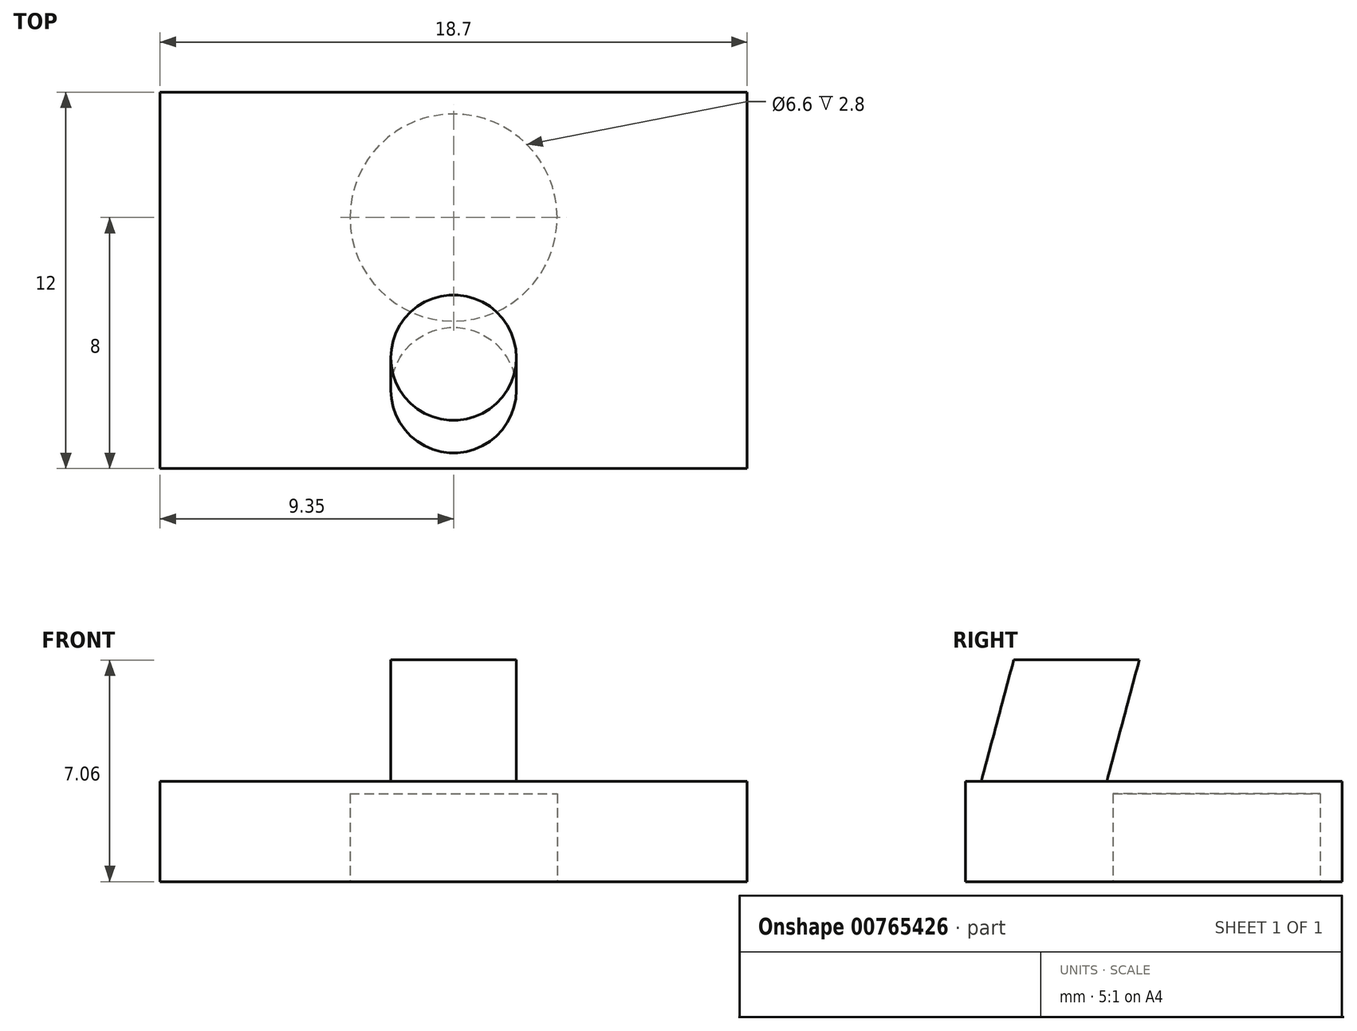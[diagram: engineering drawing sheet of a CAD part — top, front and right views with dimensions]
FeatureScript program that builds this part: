
annotation { "Feature Type Name" : "Feature", "Feature Type Description" : "" }
export const myFeature = defineFeature(function(context is Context, id is Id, definition is map)
    precondition{}
    {
        {
            var Q0;
            Q0=qCreatedBy(makeId("Top.planeOp"),FACE);
            var sketch = newSketch(context, id + "F0", { "sketchPlane" : qUnion([Q0])});
            skLineSegment(sketch, "E0.bottom", {"start": v(9.35, 6) * mm, "end": v(-9.35, 6) * mm});
            skLineSegment(sketch, "E0.top", {"start": v(9.35, -6) * mm, "end": v(-9.35, -6) * mm});
            skLineSegment(sketch, "E0.left", {"start": v(9.35, 6) * mm, "end": v(9.35, -6) * mm});
            skLineSegment(sketch, "E0.right", {"start": v(-9.35, 6) * mm, "end": v(-9.35, -6) * mm});
            skPoint(sketch, "E0.middle", {"position": v(0, 0) * mm});
            skSolve(sketch);
        }
        {
            var Q0;
            Q0 = qSketchRegion(id + "F0", true);
            extrude(context, id + "F1", {"entities" : qUnion([Q0]), "depth" : 3.2 * mm, "offsetDistance" : 25 * mm});
        }
        {
            var Q0;
            Q0=makeQuery(id+"F1.opExtrude","CAP_FACE",FACE,{"disambiguationData":[OSD([sQuery(id+"F0.wireOp",EDGE,"E0.bottom"),sQuery(id+"F0.wireOp",EDGE,"E0.top"),sQuery(id+"F0.wireOp",EDGE,"E0.left"),sQuery(id+"F0.wireOp",EDGE,"E0.right")])],"isStart":false});
            var sketch = newSketch(context, id + "F2", { "sketchPlane" : qUnion([Q0])});
            skCircle(sketch, "E1", {"center": v(0, -3.5) * mm, "radius": 2 * mm});
            skSolve(sketch);
        }
        {
            var Q0;
            Q0=makeQuery(id+"F1.opExtrude","CAP_FACE",FACE,{"disambiguationData":[OSD([sQuery(id+"F0.wireOp",EDGE,"E0.bottom"),sQuery(id+"F0.wireOp",EDGE,"E0.top"),sQuery(id+"F0.wireOp",EDGE,"E0.left"),sQuery(id+"F0.wireOp",EDGE,"E0.right")])],"isStart":true});
            var sketch = newSketch(context, id + "F3", { "sketchPlane" : qUnion([Q0])});
            skCircle(sketch, "E2", {"center": v(0, -2) * mm, "radius": 3.3 * mm});
            skSolve(sketch);
        }
        {
            var Q0;
            Q0 = qSketchRegion(id + "F3", true);
            extrude(context, id + "F4", {"entities" : qUnion([Q0]), "operationType" : NewBodyOperationType.REMOVE, "oppositeDirection" : true, "depth" : 2.8 * mm, "offsetDistance" : 25 * mm});
        }
        {
            var Q0;
            Q0=qCreatedBy(makeId("Right.planeOp"),FACE);
            var sketch = newSketch(context, id + "F5", { "sketchPlane" : qUnion([Q0])});
            skLineSegment(sketch, "E3", {"start": v(-3.5, 3.2) * mm, "end": v(-2.46, 7.06) * mm});
            skSolve(sketch);
        }
        {
            var Q0;
            Q0 = qSketchRegion(id + "F2", true);
            var Q1;
            Q1 = qConstructionFilter(qBodyType(qCreatedBy(id + "F5" ,EDGE), BodyType.WIRE), ConstructionObject.NO);
            sweep(context, id + "F6", {"operationType" : NewBodyOperationType.ADD, "profiles" : qUnion([Q0]), "path" : qUnion([Q1])});
        }
    });
